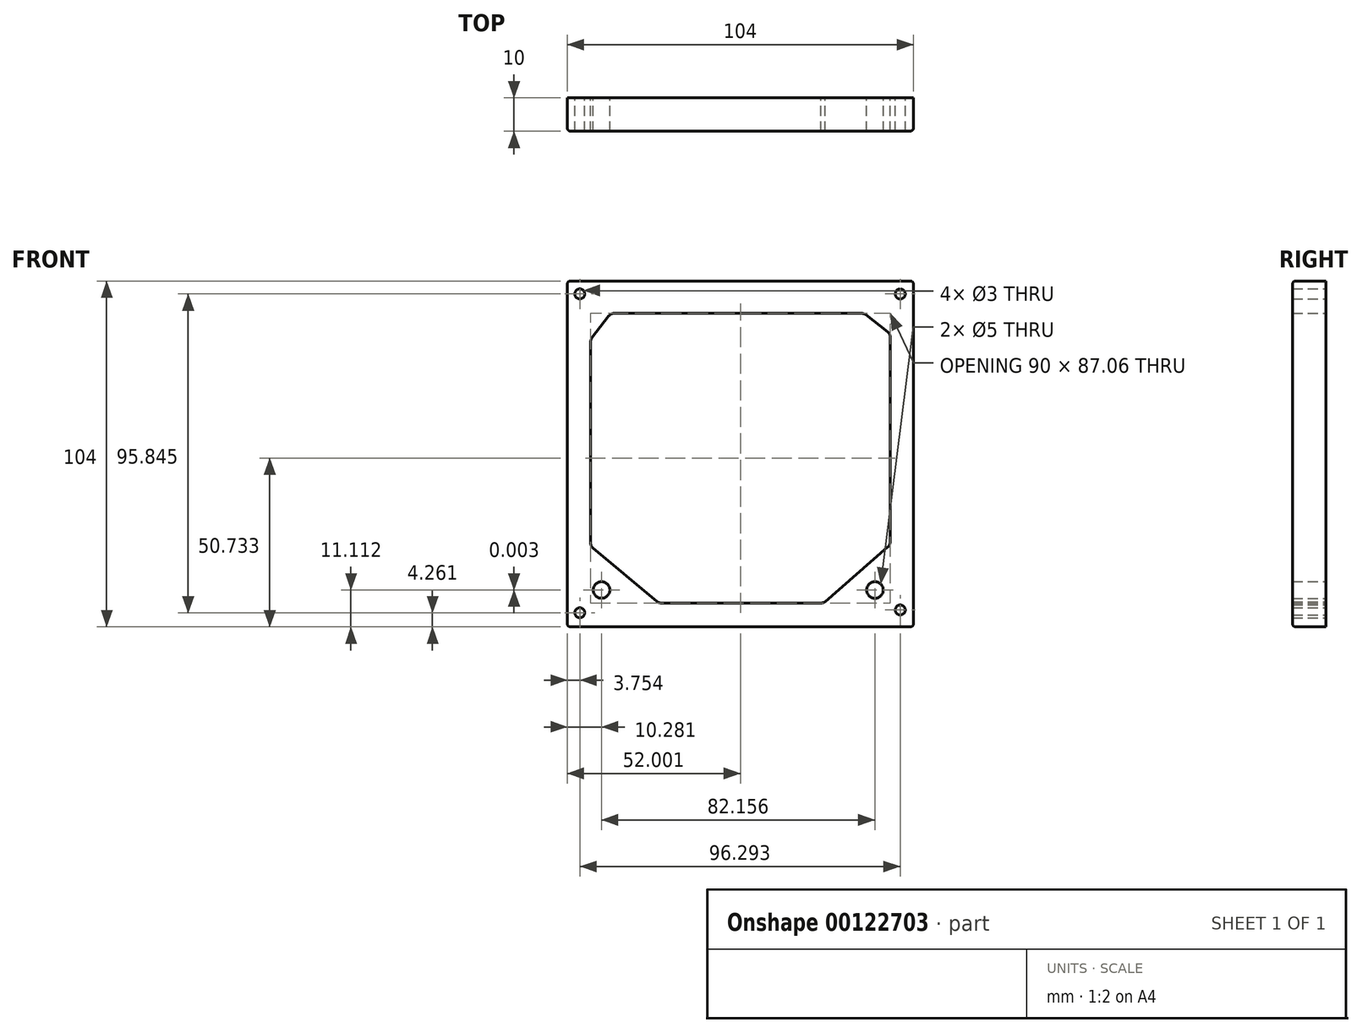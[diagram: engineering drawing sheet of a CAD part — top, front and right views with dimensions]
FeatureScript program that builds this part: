
annotation { "Feature Type Name" : "Feature", "Feature Type Description" : "" }
export const myFeature = defineFeature(function(context is Context, id is Id, definition is map)
    precondition{}
    {
        {
            var Q0;
            Q0=qCreatedBy(makeId("Front.planeOp"),FACE);
            var sketch = newSketch(context, id + "F0", { "sketchPlane" : qUnion([Q0])});
            skLineSegment(sketch, "E0.bottom", {"start": v(-50.98, 48.93) * mm, "end": v(53.02, 48.93) * mm});
            skLineSegment(sketch, "E0.top", {"start": v(-50.98, -55.07) * mm, "end": v(53.02, -55.07) * mm});
            skLineSegment(sketch, "E0.left", {"start": v(-50.98, 48.93) * mm, "end": v(-50.98, -55.07) * mm});
            skLineSegment(sketch, "E0.right", {"start": v(53.02, 48.93) * mm, "end": v(53.02, -55.07) * mm});
            skCircle(sketch, "E1", {"center": v(-47.23, 45.04) * mm, "radius": 1.5 * mm});
            skCircle(sketch, "E2", {"center": v(49.07, 45.02) * mm, "radius": 1.5 * mm});
            skCircle(sketch, "E3", {"center": v(-47.23, -50.8) * mm, "radius": 1.5 * mm});
            skCircle(sketch, "E4", {"center": v(49.07, -49.96) * mm, "radius": 1.5 * mm});
            skCircle(sketch, "E5", {"center": v(-40.7, -43.96) * mm, "radius": 2.5 * mm});
            skCircle(sketch, "E6", {"center": v(41.46, -43.96) * mm, "radius": 2.5 * mm});
            skSolve(sketch);
        }
        {
            var Q0;
            Q0=qCreatedBy(makeId("Front.planeOp"),FACE);
            var sketch = newSketch(context, id + "F1", { "sketchPlane" : qUnion([Q0])});
            skLineSegment(sketch, "E7", {"start": v(-36.9, 39.2) * mm, "end": v(37.43, 39.2) * mm});
            skLineSegment(sketch, "E8", {"start": v(46.02, 32.1) * mm, "end": v(46.02, -29.53) * mm});
            skLineSegment(sketch, "E9", {"start": v(45.34, -31.03) * mm, "end": v(26.5, -47.47) * mm});
            skLineSegment(sketch, "E10", {"start": v(25.23, -47.87) * mm, "end": v(-22.77, -47.87) * mm});
            skLineSegment(sketch, "E11", {"start": v(-24.05, -47.4) * mm, "end": v(-43.26, -31.4) * mm});
            skLineSegment(sketch, "E12", {"start": v(-43.98, -29.87) * mm, "end": v(-43.98, 30.58) * mm});
            skLineSegment(sketch, "E13", {"start": v(-43.57, 31.8) * mm, "end": v(-38.5, 38.41) * mm});
            skLineSegment(sketch, "E14", {"start": v(38.65, 38.78) * mm, "end": v(45.24, 33.68) * mm});
            skPoint(sketch, "E15.visualSharp", {"position": v(-43.98, -30.8) * mm});
            skArc(sketch, "E15.filletArc", {"start": v(-43.98, -29.87) * mm, "mid": v(-43.8, -30.72) * mm, "end": v(-43.26, -31.4) * mm});
            skPoint(sketch, "E16.visualSharp", {"position": v(-23.5, -47.87) * mm});
            skArc(sketch, "E16.filletArc", {"start": v(-24.05, -47.4) * mm, "mid": v(-23.45, -47.75) * mm, "end": v(-22.77, -47.87) * mm});
            skArc(sketch, "E17.filletArc", {"start": v(25.23, -47.87) * mm, "mid": v(25.9, -47.78) * mm, "end": v(26.5, -47.47) * mm});
            skArc(sketch, "E18.filletArc", {"start": v(45.34, -31.03) * mm, "mid": v(45.84, -30.35) * mm, "end": v(46.02, -29.53) * mm});
            skPoint(sketch, "E19.visualSharp", {"position": v(-43.98, 31.26) * mm});
            skArc(sketch, "E19.filletArc", {"start": v(-43.57, 31.8) * mm, "mid": v(-43.87, 31.23) * mm, "end": v(-43.98, 30.58) * mm});
            skPoint(sketch, "E20.visualSharp", {"position": v(-37.9, 39.2) * mm});
            skArc(sketch, "E20.filletArc", {"start": v(-36.9, 39.2) * mm, "mid": v(-37.79, 38.99) * mm, "end": v(-38.5, 38.41) * mm});
            skPoint(sketch, "E21.visualSharp", {"position": v(38.1, 39.2) * mm});
            skArc(sketch, "E21.filletArc", {"start": v(38.65, 38.78) * mm, "mid": v(38.07, 39.09) * mm, "end": v(37.43, 39.2) * mm});
            skPoint(sketch, "E22.visualSharp", {"position": v(46.02, 33.08) * mm});
            skArc(sketch, "E22.filletArc", {"start": v(46.02, 32.1) * mm, "mid": v(45.82, 32.98) * mm, "end": v(45.24, 33.68) * mm});
            skSolve(sketch);
        }
        {
            var Q0;
            Q0=makeQuery(id+"F0.imprint","IMPRINT",FACE,{"disambiguationData":[TD([[makeQuery(id+"F0.imprint","IMPRINT",EDGE,{"derivedFrom":sQuery(id+"F0.wireOp",EDGE,"E0.bottom")}),-1.0]])]});
            extrude(context, id + "F2", {"entities" : qUnion([Q0]), "depth" : 10 * mm});
        }
        {
            var Q0;
            Q0=qSketchRegion(id+"F1",true);
            var Q1;
            Q1=makeQuery(id+"F2.opExtrude","CAP_FACE",FACE,{"disambiguationData":[OSD([sQuery(id+"F0.wireOp",EDGE,"E0.bottom"),sQuery(id+"F0.wireOp",EDGE,"E0.top"),sQuery(id+"F0.wireOp",EDGE,"E0.left"),sQuery(id+"F0.wireOp",EDGE,"E0.right"),sQuery(id+"F0.wireOp",EDGE,"E1"),sQuery(id+"F0.wireOp",EDGE,"E2"),sQuery(id+"F0.wireOp",EDGE,"E3"),sQuery(id+"F0.wireOp",EDGE,"E4")])],"isStart":false});
            extrude(context, id + "F3", {"entities" : qUnion([Q0, Q1]), "operationType" : NewBodyOperationType.REMOVE, "depth" : 25 * mm});
        }
        {
            var Q0;
            Q0=makeQuery(id+"F2.opExtrude","SWEPT_EDGE",EDGE,{"disambiguationData":[OSD([sQuery(id+"F0.wireOp",EDGE,"E0.bottom"),sQuery(id+"F0.wireOp",EDGE,"E0.left")])]});
            var Q1;
            Q1=makeQuery(id+"F2.opExtrude","CAP_EDGE",EDGE,{"disambiguationData":[OSD([sQuery(id+"F0.wireOp",EDGE,"E0.left")])],"isStart":false});
            var Q2;
            Q2=makeQuery(id+"F2.opExtrude","CAP_EDGE",EDGE,{"disambiguationData":[OSD([sQuery(id+"F0.wireOp",EDGE,"E0.bottom")])],"isStart":false});
            var Q3;
            Q3=makeQuery(id+"F2.opExtrude","SWEPT_EDGE",EDGE,{"disambiguationData":[OSD([sQuery(id+"F0.wireOp",EDGE,"E0.top"),sQuery(id+"F0.wireOp",EDGE,"E0.left")])]});
            var Q4;
            Q4=makeQuery(id+"F2.opExtrude","CAP_EDGE",EDGE,{"disambiguationData":[OSD([sQuery(id+"F0.wireOp",EDGE,"E0.top")])],"isStart":false});
            var Q5;
            Q5=makeQuery(id+"F2.opExtrude","CAP_EDGE",EDGE,{"disambiguationData":[OSD([sQuery(id+"F0.wireOp",EDGE,"E0.right")])],"isStart":false});
            var Q6;
            Q6=makeQuery(id+"F2.opExtrude","SWEPT_EDGE",EDGE,{"disambiguationData":[OSD([sQuery(id+"F0.wireOp",EDGE,"E0.bottom"),sQuery(id+"F0.wireOp",EDGE,"E0.right")])]});
            var Q7;
            Q7=makeQuery(id+"F2.opExtrude","SWEPT_EDGE",EDGE,{"disambiguationData":[OSD([sQuery(id+"F0.wireOp",EDGE,"E0.top"),sQuery(id+"F0.wireOp",EDGE,"E0.right")])]});
            fillet(context, id + "F4", {"entities" : qUnion([Q0, Q1, Q2, Q3, Q4, Q5, Q6, Q7]), "radius" : 1 * mm, "tangentPropagation" : true, "allowEdgeOverflow" : false});
        }
    });
